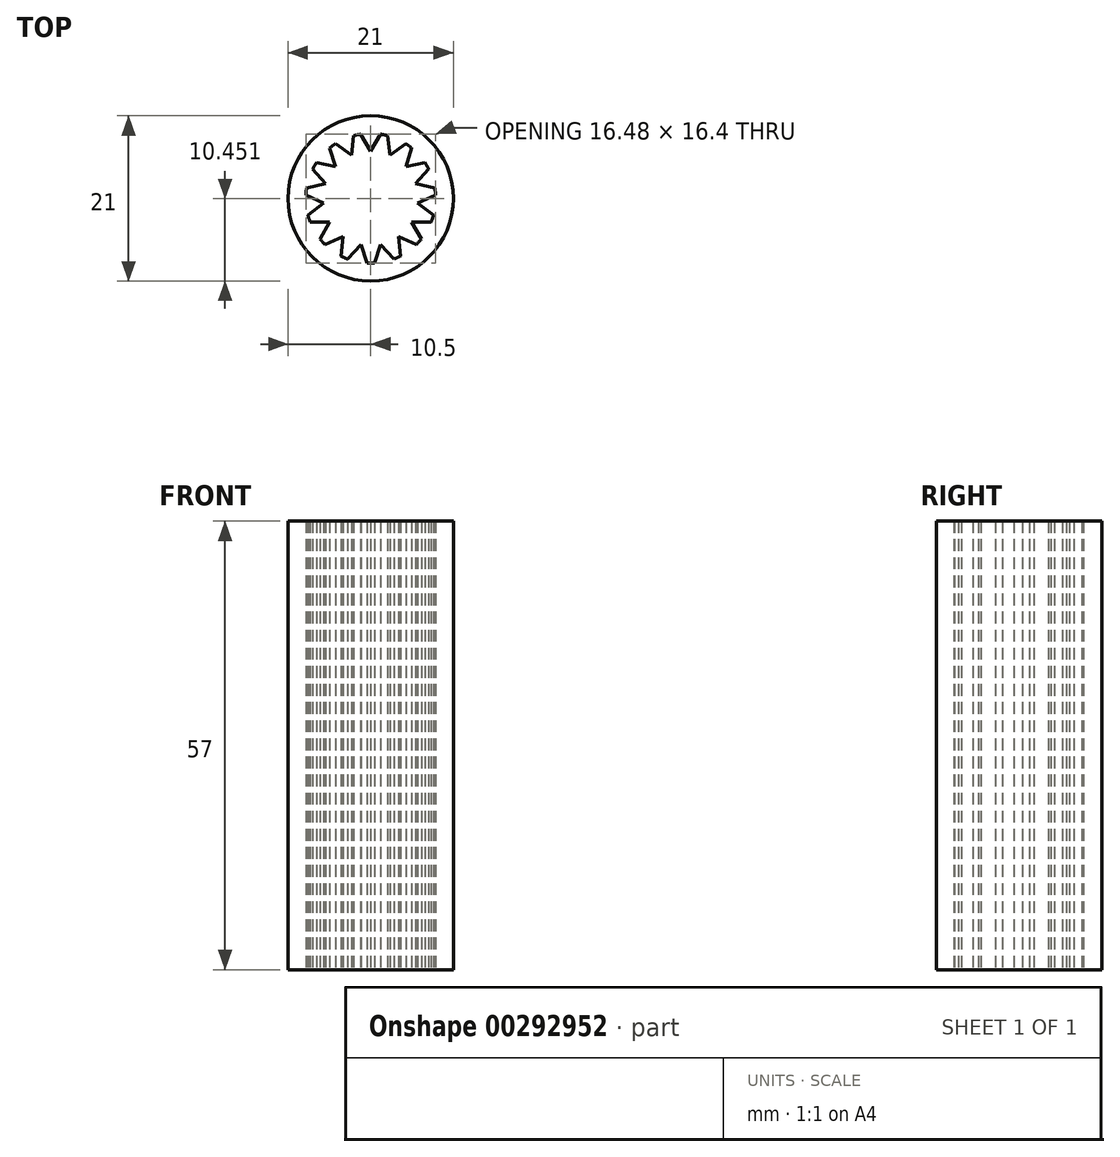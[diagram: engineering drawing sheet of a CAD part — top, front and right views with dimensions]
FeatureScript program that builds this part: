
annotation { "Feature Type Name" : "Feature", "Feature Type Description" : "" }
export const myFeature = defineFeature(function(context is Context, id is Id, definition is map)
    precondition{}
    {
        {
            var Q0;
            Q0=qCreatedBy(makeId("Top.planeOp"),FACE);
            var sketch = newSketch(context, id + "F0", { "sketchPlane" : qUnion([Q0])});
            skCircle(sketch, "E0", {"center": v(0, 0) * mm, "radius": 10.5 * mm});
            skCircle(sketch, "E1", {"center": v(0, 0) * mm, "radius": 8.25 * mm});
            skLineSegment(sketch, "E2", {"start": v(0, 6) * mm, "end": v(1.26, 8.15) * mm});
            skLineSegment(sketch, "E3", {"start": v(0, 0) * mm, "end": v(0, 10.5) * mm, "construction": true});
            skCircle(sketch, "E4", {"center": v(0, 6) * mm, "radius": 2.5 * mm, "construction": true});
            skLineSegment(sketch, "E5", {"start": v(-1.26, 8.15) * mm, "end": v(0, 6) * mm});
            skLineSegment(sketch, "E6.1.0", {"start": v(-4.47, 6.93) * mm, "end": v(-2.44, 5.48) * mm});
            skLineSegment(sketch, "E6.1.1", {"start": v(-2.44, 5.48) * mm, "end": v(-2.16, 7.96) * mm});
            skLineSegment(sketch, "E6.2.0", {"start": v(-6.9, 4.52) * mm, "end": v(-4.46, 4.01) * mm});
            skLineSegment(sketch, "E6.2.1", {"start": v(-4.46, 4.01) * mm, "end": v(-5.21, 6.4) * mm});
            skLineSegment(sketch, "E6.3.0", {"start": v(-8.14, 1.32) * mm, "end": v(-5.7, 1.85) * mm});
            skLineSegment(sketch, "E6.3.1", {"start": v(-5.7, 1.85) * mm, "end": v(-7.36, 3.72) * mm});
            skLineSegment(sketch, "E6.4.0", {"start": v(-7.98, -2.1) * mm, "end": v(-5.97, -0.63) * mm});
            skLineSegment(sketch, "E6.4.1", {"start": v(-5.97, -0.63) * mm, "end": v(-8.24, 0.4) * mm});
            skLineSegment(sketch, "E6.5.0", {"start": v(-6.43, -5.17) * mm, "end": v(-5.2, -3) * mm});
            skLineSegment(sketch, "E6.5.1", {"start": v(-5.2, -3) * mm, "end": v(-7.7, -2.98) * mm});
            skLineSegment(sketch, "E6.6.0", {"start": v(-3.77, -7.34) * mm, "end": v(-3.53, -4.85) * mm});
            skLineSegment(sketch, "E6.6.1", {"start": v(-3.53, -4.85) * mm, "end": v(-5.81, -5.85) * mm});
            skLineSegment(sketch, "E6.7.0", {"start": v(-0.46, -8.24) * mm, "end": v(-1.25, -5.87) * mm});
            skLineSegment(sketch, "E6.7.1", {"start": v(-1.25, -5.87) * mm, "end": v(-2.93, -7.71) * mm});
            skLineSegment(sketch, "E6.8.0", {"start": v(2.93, -7.71) * mm, "end": v(1.25, -5.87) * mm});
            skLineSegment(sketch, "E6.8.1", {"start": v(1.25, -5.87) * mm, "end": v(0.46, -8.24) * mm});
            skLineSegment(sketch, "E6.9.0", {"start": v(5.81, -5.85) * mm, "end": v(3.53, -4.85) * mm});
            skLineSegment(sketch, "E6.9.1", {"start": v(3.53, -4.85) * mm, "end": v(3.77, -7.34) * mm});
            skLineSegment(sketch, "E6.10.0", {"start": v(7.7, -2.98) * mm, "end": v(5.2, -3) * mm});
            skLineSegment(sketch, "E6.10.1", {"start": v(5.2, -3) * mm, "end": v(6.43, -5.17) * mm});
            skLineSegment(sketch, "E7.2.11.0", {"start": v(8.24, 0.4) * mm, "end": v(5.97, -0.63) * mm});
            skLineSegment(sketch, "E7.3.11.0", {"start": v(5.97, -0.63) * mm, "end": v(7.98, -2.1) * mm});
            skLineSegment(sketch, "E8.2.12.0", {"start": v(7.36, 3.72) * mm, "end": v(5.7, 1.85) * mm});
            skLineSegment(sketch, "E8.3.12.0", {"start": v(5.7, 1.85) * mm, "end": v(8.14, 1.32) * mm});
            skLineSegment(sketch, "E9.2.13.0", {"start": v(5.21, 6.4) * mm, "end": v(4.46, 4.01) * mm});
            skLineSegment(sketch, "E9.3.13.0", {"start": v(4.46, 4.01) * mm, "end": v(6.9, 4.52) * mm});
            skLineSegment(sketch, "E10.2.14.0", {"start": v(2.16, 7.96) * mm, "end": v(2.44, 5.48) * mm});
            skLineSegment(sketch, "E10.3.14.0", {"start": v(2.44, 5.48) * mm, "end": v(4.47, 6.93) * mm});
            skCircle(sketch, "E11", {"center": v(0, 0) * mm, "radius": 6 * mm, "construction": true});
            skSolve(sketch);
        }
        {
            var Q0;
            Q0=makeQuery(id+"F0.imprint","IMPRINT",FACE,{"disambiguationData":[TD([[makeQuery(id+"F0.imprint","IMPRINT",EDGE,{"derivedFrom":sQuery(id+"F0.wireOp",EDGE,"E0")}),1.0]])]});
            var Q1;
            {var subQ0=sQuery(id+"F0.wireOp",EDGE,"E6.3.0");Q1=makeQuery(id+"F0.imprint","IMPRINT",FACE,{"disambiguationData":[TD([[makeQuery(id+"F0.imprint","IMPRINT",EDGE,{"derivedFrom":subQ0}),1.0]])]});}
            var Q2;
            {var subQ0=sQuery(id+"F0.wireOp",EDGE,"E6.2.0");Q2=makeQuery(id+"F0.imprint","IMPRINT",FACE,{"disambiguationData":[TD([[makeQuery(id+"F0.imprint","IMPRINT",EDGE,{"derivedFrom":subQ0}),1.0]])]});}
            var Q3;
            {var subQ0=sQuery(id+"F0.wireOp",EDGE,"E6.1.0");Q3=makeQuery(id+"F0.imprint","IMPRINT",FACE,{"disambiguationData":[TD([[makeQuery(id+"F0.imprint","IMPRINT",EDGE,{"derivedFrom":subQ0}),1.0]])]});}
            var Q4;
            {var subQ0=sQuery(id+"F0.wireOp",EDGE,"E2");Q4=makeQuery(id+"F0.imprint","IMPRINT",FACE,{"disambiguationData":[TD([[makeQuery(id+"F0.imprint","IMPRINT",EDGE,{"derivedFrom":subQ0}),1.0]])]});}
            var Q5;
            {var subQ0=sQuery(id+"F0.wireOp",EDGE,"E10.2.14.0");Q5=makeQuery(id+"F0.imprint","IMPRINT",FACE,{"disambiguationData":[TD([[makeQuery(id+"F0.imprint","IMPRINT",EDGE,{"derivedFrom":subQ0}),1.0]])]});}
            var Q6;
            {var subQ0=sQuery(id+"F0.wireOp",EDGE,"E9.2.13.0");Q6=makeQuery(id+"F0.imprint","IMPRINT",FACE,{"disambiguationData":[TD([[makeQuery(id+"F0.imprint","IMPRINT",EDGE,{"derivedFrom":subQ0}),1.0]])]});}
            var Q7;
            {var subQ0=sQuery(id+"F0.wireOp",EDGE,"E8.2.12.0");Q7=makeQuery(id+"F0.imprint","IMPRINT",FACE,{"disambiguationData":[TD([[makeQuery(id+"F0.imprint","IMPRINT",EDGE,{"derivedFrom":subQ0}),1.0]])]});}
            var Q8;
            {var subQ0=sQuery(id+"F0.wireOp",EDGE,"E7.2.11.0");Q8=makeQuery(id+"F0.imprint","IMPRINT",FACE,{"disambiguationData":[TD([[makeQuery(id+"F0.imprint","IMPRINT",EDGE,{"derivedFrom":subQ0}),1.0]])]});}
            var Q9;
            {var subQ0=sQuery(id+"F0.wireOp",EDGE,"E6.10.0");Q9=makeQuery(id+"F0.imprint","IMPRINT",FACE,{"disambiguationData":[TD([[makeQuery(id+"F0.imprint","IMPRINT",EDGE,{"derivedFrom":subQ0}),1.0]])]});}
            var Q10;
            {var subQ0=sQuery(id+"F0.wireOp",EDGE,"E6.9.0");Q10=makeQuery(id+"F0.imprint","IMPRINT",FACE,{"disambiguationData":[TD([[makeQuery(id+"F0.imprint","IMPRINT",EDGE,{"derivedFrom":subQ0}),1.0]])]});}
            var Q11;
            {var subQ0=sQuery(id+"F0.wireOp",EDGE,"E6.8.0");Q11=makeQuery(id+"F0.imprint","IMPRINT",FACE,{"disambiguationData":[TD([[makeQuery(id+"F0.imprint","IMPRINT",EDGE,{"derivedFrom":subQ0}),1.0]])]});}
            var Q12;
            {var subQ0=sQuery(id+"F0.wireOp",EDGE,"E6.7.0");Q12=makeQuery(id+"F0.imprint","IMPRINT",FACE,{"disambiguationData":[TD([[makeQuery(id+"F0.imprint","IMPRINT",EDGE,{"derivedFrom":subQ0}),1.0]])]});}
            var Q13;
            {var subQ0=sQuery(id+"F0.wireOp",EDGE,"E6.6.0");Q13=makeQuery(id+"F0.imprint","IMPRINT",FACE,{"disambiguationData":[TD([[makeQuery(id+"F0.imprint","IMPRINT",EDGE,{"derivedFrom":subQ0}),1.0]])]});}
            var Q14;
            {var subQ0=sQuery(id+"F0.wireOp",EDGE,"E6.5.0");Q14=makeQuery(id+"F0.imprint","IMPRINT",FACE,{"disambiguationData":[TD([[makeQuery(id+"F0.imprint","IMPRINT",EDGE,{"derivedFrom":subQ0}),1.0]])]});}
            var Q15;
            {var subQ0=sQuery(id+"F0.wireOp",EDGE,"E6.4.0");Q15=makeQuery(id+"F0.imprint","IMPRINT",FACE,{"disambiguationData":[TD([[makeQuery(id+"F0.imprint","IMPRINT",EDGE,{"derivedFrom":subQ0}),1.0]])]});}
            extrude(context, id + "F1", {"entities" : qUnion([Q0, Q1, Q2, Q3, Q4, Q5, Q6, Q7, Q8, Q9, Q10, Q11, Q12, Q13, Q14, Q15]), "depth" : 57 * mm});
        }
    });
